# Revit family: 2CKA000230A0411
name_source: partatom
category: Elektroinstallationen
revit_build: Autodesk Revit 2017 (Build: 20160225_1515(x64)
units: mm (PartAtom-declared; Revit-internal decimal feet)

## family parameters
Basisbauteil = Fläche
Beim Laden mit Abzugskörper schneiden = Nein
Bemaßung runder Anschluss = Durchmesser verwenden
Beschriftungsausrichtung beibehalten = Nein
Gemeinsam genutzt = Nein
Raumberechnungspunkt = Nein
Teiletyp = Normal

## types (1)
- 2CKA000230A0411
    Anschlussart = LSA
    Aufputz = Ja
    BIM = https://media.live.bim.site
    BIMSITE_PRODUCT_ID = 41f529de7edb1520624726aed988ee83d9b20691
    Befestigungsart = schrauben
    Beschreibung = UAE-Anschlussdose, RJ45, Cat. 6a iso, geschirmt, UP-Montagedosen und -Einsätze, Einsätze für Datenkommunikation, UAE-Anschlussdose, RJ45, Cat. 6a iso, geschirmt 2 Steckbuchsen, 8/8-polig Mit Schrägauslass und LSA-Schneidklemmen. RJ-45-Anschlüsse für Netzwerke nach Cat. 6A, Class EA (10 Gbit/s / 500 MHz). Entspricht Cat. 6A, Class EA gem. ISO/IEC 11801:2011-06. Anschlusskennzeichnung A und B gemäß TIA/EIA-568-B.2. Bauart nach EN 60 603-7-51:2011-01. Abschirmung nach DIN EN 55022, Klasse B. Bis 500 MHz auf allen Aderpaaren. Geeignet für 10-Gigabit Ethernet. Geeignet für PoE+ gemäß IEEE 802.3at, ? 1000 Steckzyklen. Flexible Kabelzuführung ohne Knicke von allen Seiten. Gehäuse-Erdung mittels 6,3 mm-Flachsteckverbinder rückseitig möglich. Re-embedded getestet. Geeiget für Mix-and-Match-Einsatz. Geeignet für RJ 11, RJ 12 und RJ 45 Stecker. Für Datenkabel mit einem Durchmesser von 6-10 mm. Für Montage in Kabelkanälen, UP-Gerätedosen und Unterflursystemen. Für Adern von AWG 24-22. Ohne Spreize. Einbautiefe 31 mm.
    Bodentank/Unterflurmontage = Ja
    Buchsen geschirmt = Ja
    Datenblatt = https://media.live.bim.site BJE_DinA4-Online_dut.pdf
    Datenblatt 1 = https://media.live.bim.site BJE_DinA4-Online_eng.pdf
    Datenblatt 2 = https://media.live.bim.site BJE_DinA4-Online_ger.pdf
    Datenblatt 3 = https://media.live.bim.site
    Designfähig = Ja
    Farbe = weiß
    GTIN = 4011395163870
    Geeignet für Anzahl Buchsen/Kupplungen = 2
    Gehäuse geschirmt = Ja
    HAN = 2CKA000230A0411
    HeinzeBIM = https://www.heinze.de
    Hersteller = Busch-Jaeger
    Ist System = Nein
    Ist Zubehör = Nein
    Kanaleinbau = Ja
    Kategorie = 6A (IEC)
    Montageart Schirmanschluss = Schraube
    RAL-Nummer (ähnlich) = 9010
    Schutzart (IP) = IP20
    Separate Kabelzugentlastung = Ja
    Separater Erdungsanschluss = Ja
    Steckverbindertyp = RJ45 8(8)
    TYPE = 0218/12-101
    Typname = UAE-Anschlussdose, RJ45, Cat. 6a iso, geschirmt, UP-Montagedosen und -Einsätze, Einsätze für Datenkommunikation
    URL = https://www.busch-jaeger.de
    Unterputz = Ja
    Vorgabe-Ansicht = 1219 mm
    White = White

## geometry (parser evidence)
native form markers: Sweep x3
no freeform markers — native parametric forms only
